# Revit family: Storage-Teknion-AFML_Audience_Laminate_Hospitality_Cart-R2023
name_source: partatom
category: Furniture
units: mm (PartAtom-declared; Revit-internal decimal feet)

## family parameters
Always vertical = Yes
Cut with Voids When Loaded = No
Enable Cutting in Views = No
OmniClass Number = 23.40.20.00
OmniClass Title = General Furniture and Specialties
Render Appearance Source = Family Geometry
Room Calculation Point = No
Shared = Yes
Work Plane-Based = No

## types (2) — shared parameters
Assembly Code = E2020200
Manufacturer = Teknion
Manufacturer Fax = 416.661.4586
Part Number = AFML
Product Documentation Link = https://www.teknion.com
Product Line = Storage
Product Page URL = https://www.teknion.com
Series = Audience Boardroom Storage
Sustainability Data = https://www.teknion.com
Two Handle = Yes
URL = www.teknion.com
Unit Weight URL = http://www.teknion.com
Warranty = http://www.teknion.com
zero-valued in all types: Default Elevation

## per-type parameters (varying)
| type | Cutout Offset | Description | Model | One Handle | Solid Doors | Solid Doors and Drawers | Two Door | Two Handle High | Two Handle Low |
| Door Configuration | 33.599 " | Audience Laminate Hospitality Cart, Doors Configuration, Solid Door Style, 32" Width, 36" Height | AFMLAS3236 | No | Yes | No | Yes | Yes | No |
| Door & Drawers Configuration | 29.357 " | Audience Laminate Hospitality Cart, Doors & Drawers Configuration, Solid Door Style, 32" Width, 36" Height | AFMLBS3236 | Yes | No | Yes | No | No | Yes |

## geometry (parser evidence)
native form markers: Sweep x2
no freeform markers — native parametric forms only
